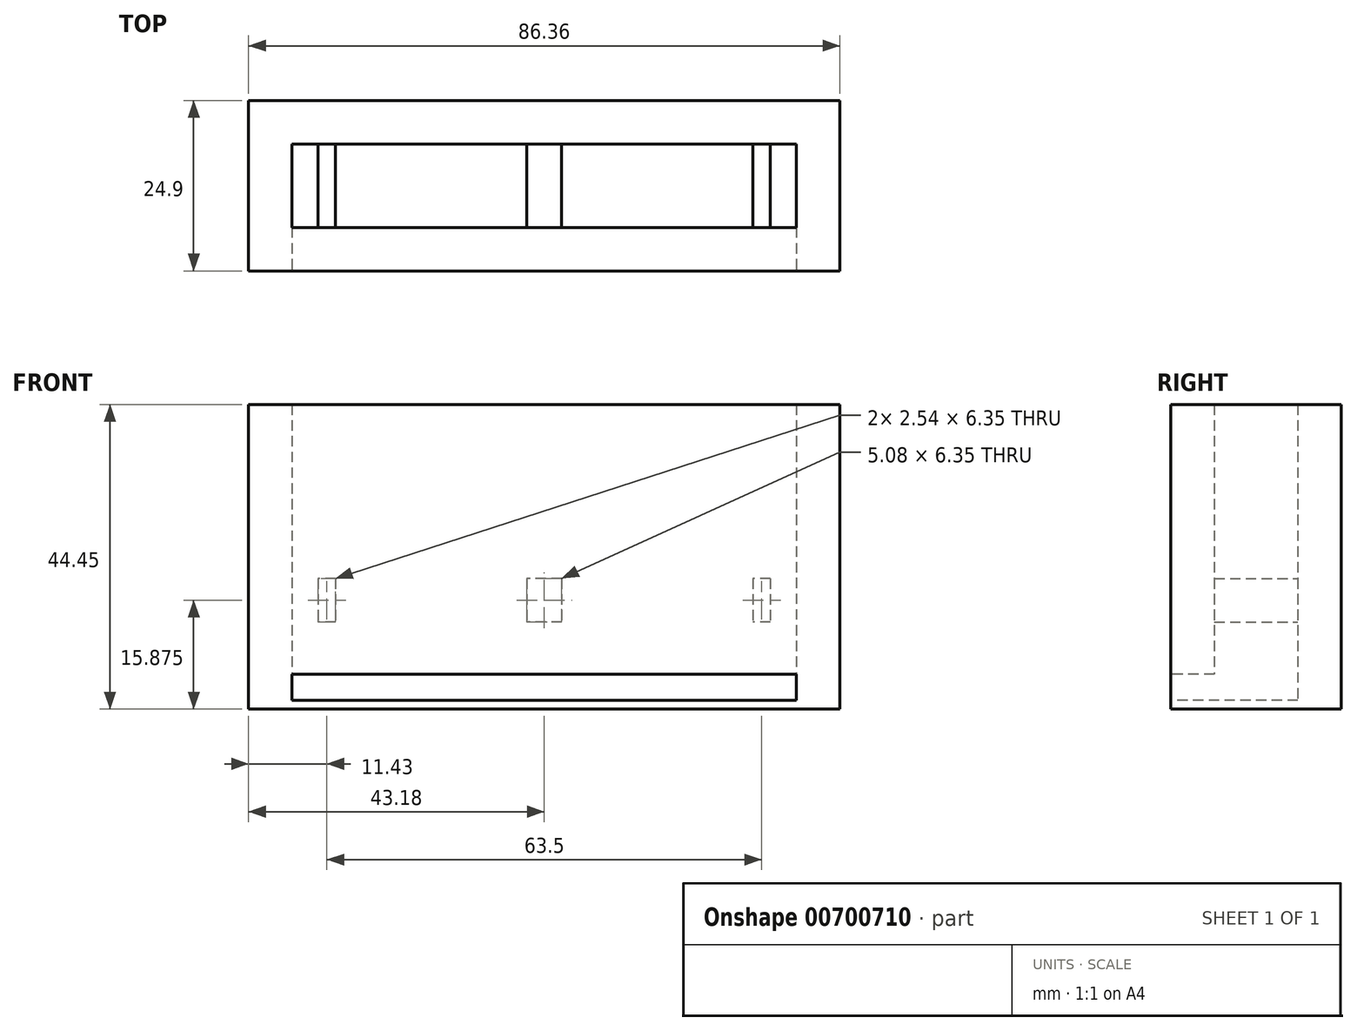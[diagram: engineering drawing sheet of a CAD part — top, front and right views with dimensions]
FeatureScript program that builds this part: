
annotation { "Feature Type Name" : "Feature", "Feature Type Description" : "" }
export const myFeature = defineFeature(function(context is Context, id is Id, definition is map)
    precondition{}
    {
        {
            var Q0;
            Q0=qCreatedBy(makeId("Top.planeOp"),FACE);
            var sketch = newSketch(context, id + "F0", { "sketchPlane" : qUnion([Q0])});
            skLineSegment(sketch, "E0.bottom", {"start": v(36.83, 6.1) * mm, "end": v(-36.83, 6.1) * mm});
            skLineSegment(sketch, "E0.top", {"start": v(36.83, -6.1) * mm, "end": v(-36.83, -6.1) * mm});
            skLineSegment(sketch, "E0.left", {"start": v(36.83, 6.1) * mm, "end": v(36.83, -6.1) * mm});
            skLineSegment(sketch, "E0.right", {"start": v(-36.83, 6.1) * mm, "end": v(-36.83, -6.1) * mm});
            skPoint(sketch, "E0.middle", {"position": v(0, 0) * mm});
            skLineSegment(sketch, "E1.bottom", {"start": v(43.18, 12.45) * mm, "end": v(-43.18, 12.45) * mm});
            skLineSegment(sketch, "E1.top", {"start": v(43.18, -12.45) * mm, "end": v(-43.18, -12.45) * mm});
            skLineSegment(sketch, "E1.left", {"start": v(43.18, 12.45) * mm, "end": v(43.18, -12.45) * mm});
            skLineSegment(sketch, "E1.right", {"start": v(-43.18, 12.45) * mm, "end": v(-43.18, -12.45) * mm});
            skSolve(sketch);
        }
        {
            var Q0;
            Q0=makeQuery(id+"F0.imprint","IMPRINT",FACE,{"disambiguationData":[TD([[makeQuery(id+"F0.imprint","IMPRINT",EDGE,{"derivedFrom":sQuery(id+"F0.wireOp",EDGE,"E0.bottom")}),-1.0]])]});
            extrude(context, id + "F1", {"entities" : qUnion([Q0]), "depth" : 19.05 * mm, "offsetDistance" : 25.4 * mm});
        }
        {
            var Q0;
            Q0=makeQuery(id+"F1.opExtrude","CAP_FACE",FACE,{"disambiguationData":[OSD([sQuery(id+"F0.wireOp",EDGE,"E0.bottom"),sQuery(id+"F0.wireOp",EDGE,"E0.top"),sQuery(id+"F0.wireOp",EDGE,"E0.left"),sQuery(id+"F0.wireOp",EDGE,"E0.right"),sQuery(id+"F0.wireOp",EDGE,"E1.bottom"),sQuery(id+"F0.wireOp",EDGE,"E1.top"),sQuery(id+"F0.wireOp",EDGE,"E1.left"),sQuery(id+"F0.wireOp",EDGE,"E1.right")])],"isStart":true});
            extrude(context, id + "F2", {"entities" : qUnion([Q0]), "operationType" : NewBodyOperationType.ADD, "depth" : 12.7 * mm, "offsetDistance" : 25.4 * mm});
        }
        {
            var Q0;
            Q0=makeQuery(id+"F2.opExtrude","CAP_FACE",FACE,{"disambiguationData":[OSD([sQuery(id+"F0.wireOp",EDGE,"E0.bottom"),sQuery(id+"F0.wireOp",EDGE,"E0.top"),sQuery(id+"F0.wireOp",EDGE,"E0.left"),sQuery(id+"F0.wireOp",EDGE,"E0.right"),sQuery(id+"F0.wireOp",EDGE,"E1.bottom"),sQuery(id+"F0.wireOp",EDGE,"E1.top"),sQuery(id+"F0.wireOp",EDGE,"E1.left"),sQuery(id+"F0.wireOp",EDGE,"E1.right")])],"isStart":false});
            var sketch = newSketch(context, id + "F3", { "sketchPlane" : qUnion([Q0])});
            skLineSegment(sketch, "E2.bottom", {"start": v(-43.18, -12.45) * mm, "end": v(43.18, -12.45) * mm});
            skLineSegment(sketch, "E2.top", {"start": v(-43.18, 12.45) * mm, "end": v(43.18, 12.45) * mm});
            skLineSegment(sketch, "E2.left", {"start": v(-43.18, -12.45) * mm, "end": v(-43.18, 12.45) * mm});
            skLineSegment(sketch, "E2.right", {"start": v(43.18, -12.45) * mm, "end": v(43.18, 12.45) * mm});
            skLineSegment(sketch, "E3.bottom", {"start": v(2.54, 6.1) * mm, "end": v(-2.54, 6.1) * mm});
            skLineSegment(sketch, "E3.top", {"start": v(2.54, -6.1) * mm, "end": v(-2.54, -6.1) * mm});
            skLineSegment(sketch, "E3.left", {"start": v(2.54, 6.1) * mm, "end": v(2.54, -6.1) * mm});
            skLineSegment(sketch, "E3.right", {"start": v(-2.54, 6.1) * mm, "end": v(-2.54, -6.1) * mm});
            skPoint(sketch, "E3.middle", {"position": v(0, 0) * mm});
            skLineSegment(sketch, "E4.bottom", {"start": v(-30.48, 6.1) * mm, "end": v(-33.02, 6.1) * mm});
            skLineSegment(sketch, "E4.top", {"start": v(-30.48, -6.1) * mm, "end": v(-33.02, -6.1) * mm});
            skLineSegment(sketch, "E4.left", {"start": v(-30.48, 6.1) * mm, "end": v(-30.48, -6.1) * mm});
            skLineSegment(sketch, "E4.right", {"start": v(-33.02, 6.1) * mm, "end": v(-33.02, -6.1) * mm});
            skPoint(sketch, "E4.middle", {"position": v(-31.75, 0) * mm});
            skLineSegment(sketch, "E5.bottom", {"start": v(33.02, 6.1) * mm, "end": v(30.48, 6.1) * mm});
            skLineSegment(sketch, "E5.top", {"start": v(33.02, -6.1) * mm, "end": v(30.48, -6.1) * mm});
            skLineSegment(sketch, "E5.left", {"start": v(33.02, 6.1) * mm, "end": v(33.02, -6.1) * mm});
            skLineSegment(sketch, "E5.right", {"start": v(30.48, 6.1) * mm, "end": v(30.48, -6.1) * mm});
            skPoint(sketch, "E5.middle", {"position": v(31.75, 0) * mm});
            skSolve(sketch);
        }
        {
            var Q0;
            Q0=makeQuery(id+"F3.imprint","IMPRINT",FACE,{"disambiguationData":[TD([[makeQuery(id+"F3.imprint","IMPRINT",EDGE,{"derivedFrom":sQuery(id+"F3.wireOp",EDGE,"E4.bottom")}),1.0]])]});
            var Q1;
            Q1=makeQuery(id+"F3.imprint","IMPRINT",FACE,{"disambiguationData":[TD([[makeQuery(id+"F3.imprint","IMPRINT",EDGE,{"derivedFrom":sQuery(id+"F3.wireOp",EDGE,"E3.bottom")}),1.0]])]});
            var Q2;
            Q2=makeQuery(id+"F3.imprint","IMPRINT",FACE,{"disambiguationData":[TD([[makeQuery(id+"F3.imprint","IMPRINT",EDGE,{"derivedFrom":sQuery(id+"F3.wireOp",EDGE,"E5.bottom")}),1.0]])]});
            extrude(context, id + "F4", {"entities" : qUnion([Q0, Q1, Q2]), "operationType" : NewBodyOperationType.ADD, "oppositeDirection" : true, "depth" : 6.35 * mm, "offsetDistance" : 25.4 * mm});
        }
        {
            var Q0;
            Q0=makeQuery(id+"F3.imprint","IMPRINT",FACE,{"disambiguationData":[TD([[makeQuery(id+"F3.imprint","IMPRINT",EDGE,{"derivedFrom":sQuery(id+"F3.wireOp",EDGE,"E2.bottom")}),-1.0]])]});
            extrude(context, id + "F5", {"entities" : qUnion([Q0]), "operationType" : NewBodyOperationType.ADD, "depth" : 12.7 * mm, "offsetDistance" : 25.4 * mm});
        }
        {
            var Q0;
            {var subQ0=sQuery(id+"F0.wireOp",EDGE,"E1.top");Q0=makeQuery(id+"F5.boolean.opBoolean","MERGE",FACE,{"derivedFrom":[makeQuery(id+"F2.boolean.opBoolean","MERGE",FACE,{"derivedFrom":[makeQuery(id+"F1.opExtrude","SWEPT_FACE",FACE,{"disambiguationData":[OSD([subQ0])]}),makeQuery(id+"F2.opExtrude","SWEPT_FACE",FACE,{"disambiguationData":[OSD([subQ0])]})]}),makeQuery(id+"F5.opExtrude","SWEPT_FACE",FACE,{"disambiguationData":[OSD([sQuery(id+"F3.wireOp",EDGE,"E2.top")])]})]});}
            var sketch = newSketch(context, id + "F6", { "sketchPlane" : qUnion([Q0])});
            skLineSegment(sketch, "E6.bottom", {"start": v(36.83, -24.13) * mm, "end": v(-36.83, -24.13) * mm});
            skLineSegment(sketch, "E6.top", {"start": v(36.83, -20.32) * mm, "end": v(-36.83, -20.32) * mm});
            skLineSegment(sketch, "E6.left", {"start": v(36.83, -24.13) * mm, "end": v(36.83, -20.32) * mm});
            skLineSegment(sketch, "E6.right", {"start": v(-36.83, -24.13) * mm, "end": v(-36.83, -20.32) * mm});
            skPoint(sketch, "E6.middle", {"position": v(0, -22.23) * mm});
            skSolve(sketch);
        }
        {
            var Q0;
            Q0=makeQuery(id+"FTzdqgx5J7ccIae_1.boolean.opBoolean","MERGE",FACE,{"derivedFrom":[makeQuery(id+"F7rvIf1QOv3C7wG_1.boolean.opBoolean","MERGE",FACE,{"derivedFrom":[makeQuery(id+"F5.opExtrude","CAP_FACE",FACE,{"disambiguationData":[OSD([sQuery(id+"F0.wireOp",EDGE,"E0.bottom"),sQuery(id+"F0.wireOp",EDGE,"E0.top"),sQuery(id+"F0.wireOp",EDGE,"E0.left"),sQuery(id+"F0.wireOp",EDGE,"E0.right"),sQuery(id+"F3.wireOp",EDGE,"E2.bottom"),sQuery(id+"F3.wireOp",EDGE,"E2.top"),sQuery(id+"F3.wireOp",EDGE,"E2.left"),sQuery(id+"F3.wireOp",EDGE,"E2.right"),sQuery(id+"F3.wireOp",EDGE,"E3.bottom"),sQuery(id+"F3.wireOp",EDGE,"E3.top"),sQuery(id+"F3.wireOp",EDGE,"E4.bottom"),sQuery(id+"F3.wireOp",EDGE,"E4.top"),sQuery(id+"F3.wireOp",EDGE,"E5.bottom"),sQuery(id+"F3.wireOp",EDGE,"E5.top")])],"isStart":false}),makeQuery(id+"F7rvIf1QOv3C7wG_1.opExtrude","SWEPT_FACE",FACE,{"disambiguationData":[OSD([sQuery(id+"F6.wireOp",EDGE,"xym2wZu9-z5yY-pW2h-nHYt-AFBxwuzyhF2x.bottom")])]})]}),makeQuery(id+"FTzdqgx5J7ccIae_1.opExtrude","SWEPT_FACE",FACE,{"disambiguationData":[OSD([sQuery(id+"F6dSAF4QHwftn4x_1.wireOp",EDGE,"N9NbbaGS-yKEU-mHG9-t7eJ-3yf6dlDt5CtE.bottom")])]})]});
            var sketch = newSketch(context, id + "F7", { "sketchPlane" : qUnion([Q0])});
            skLineSegment(sketch, "E7.bottom", {"start": v(-36.83, 6.1) * mm, "end": v(36.83, 6.1) * mm});
            skLineSegment(sketch, "E7.top", {"start": v(-36.83, -6.1) * mm, "end": v(36.83, -6.1) * mm});
            skLineSegment(sketch, "E7.left", {"start": v(-36.83, 6.1) * mm, "end": v(-36.83, -6.1) * mm});
            skLineSegment(sketch, "E7.right", {"start": v(36.83, 6.1) * mm, "end": v(36.83, -6.1) * mm});
            skSolve(sketch);
        }
        {
            var Q0;
            Q0=makeQuery(id+"F7.imprint","IMPRINT",FACE,{"disambiguationData":[TD([[makeQuery(id+"F7.imprint","IMPRINT",EDGE,{"derivedFrom":sQuery(id+"F7.wireOp",EDGE,"E7.bottom")}),1.0]])]});
            extrude(context, id + "F8", {"entities" : qUnion([Q0]), "operationType" : NewBodyOperationType.ADD, "oppositeDirection" : true, "depth" : 2.54 * mm, "offsetDistance" : 25.4 * mm});
        }
        {
            var Q0;
            Q0=makeQuery(id+"F6.imprint","IMPRINT",FACE,{"disambiguationData":[TD([[makeQuery(id+"F6.imprint","IMPRINT",EDGE,{"derivedFrom":sQuery(id+"F6.wireOp",EDGE,"E6.bottom")}),-1.0]])]});
            extrude(context, id + "F9", {"entities" : qUnion([Q0]), "operationType" : NewBodyOperationType.REMOVE, "oppositeDirection" : true, "depth" : 18.54 * mm, "offsetDistance" : 25.4 * mm});
        }
    });
